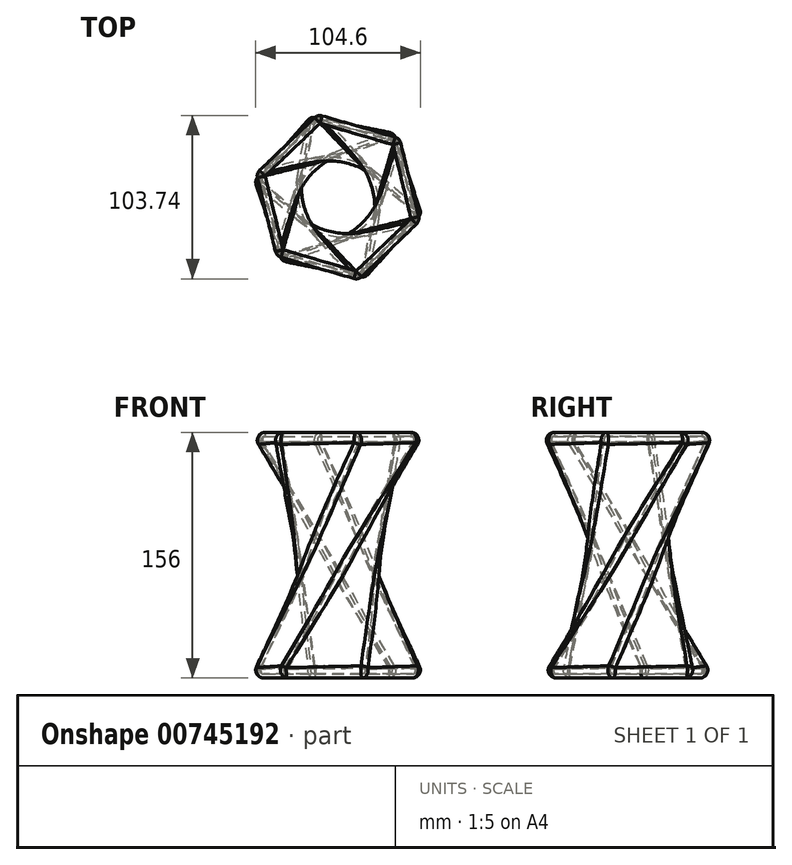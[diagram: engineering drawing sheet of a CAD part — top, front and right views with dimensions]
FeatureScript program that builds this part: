
annotation { "Feature Type Name" : "Feature", "Feature Type Description" : "" }
export const myFeature = defineFeature(function(context is Context, id is Id, definition is map)
    precondition{}
    {
        {
            var Q0;
            Q0=qCreatedBy(makeId("Top.planeOp"),FACE);
            var sketch = newSketch(context, id + "F0", { "sketchPlane" : qUnion([Q0])});
            skCircle(sketch, "E0.cCircle", {"center": v(0, 0) * mm, "radius": 49.72 * mm, "construction": true});
            skLineSegment(sketch, "E0.0", {"start": v(55.75, -13.73) * mm, "end": v(15.99, -55.14) * mm});
            skLineSegment(sketch, "E0.1", {"start": v(15.99, -55.14) * mm, "end": v(-39.76, -41.42) * mm});
            skLineSegment(sketch, "E0.2", {"start": v(-39.76, -41.42) * mm, "end": v(-55.75, 13.73) * mm});
            skLineSegment(sketch, "E0.3", {"start": v(-55.75, 13.73) * mm, "end": v(-15.99, 55.14) * mm});
            skLineSegment(sketch, "E0.4", {"start": v(-15.99, 55.14) * mm, "end": v(39.76, 41.42) * mm});
            skLineSegment(sketch, "E0.5", {"start": v(39.76, 41.42) * mm, "end": v(55.75, -13.73) * mm});
            skPoint(sketch, "E0.0.midPoint", {"position": v(35.87, -34.44) * mm});
            skSolve(sketch);
        }
        {
            var Q0;
            Q0=qCreatedBy(makeId("Top.planeOp"),FACE);
            cPlane(context, id + "F1", {"entities" : qUnion([Q0]), "cplaneType" : CPlaneType.OFFSET, "offset" : 156 * mm, "width" : 150 * mm, "height" : 150 * mm});
        }
        {
            var Q0;
            Q0=qCreatedBy(id+"F1.planeOp",FACE);
            var sketch = newSketch(context, id + "F2", { "sketchPlane" : qUnion([Q0])});
            skLineSegment(sketch, "E1.0.0", {"start": v(55.75, -13.73) * mm, "end": v(39.76, 41.42) * mm});
            skLineSegment(sketch, "E1.0.1", {"start": v(39.76, 41.42) * mm, "end": v(-15.99, 55.14) * mm});
            skLineSegment(sketch, "E1.0.2", {"start": v(-15.99, 55.14) * mm, "end": v(-55.75, 13.73) * mm});
            skLineSegment(sketch, "E1.0.3", {"start": v(-55.75, 13.73) * mm, "end": v(-39.76, -41.42) * mm});
            skLineSegment(sketch, "E1.0.4", {"start": v(-39.76, -41.42) * mm, "end": v(15.99, -55.14) * mm});
            skLineSegment(sketch, "E1.0.5", {"start": v(15.99, -55.14) * mm, "end": v(55.75, -13.73) * mm});
            skSolve(sketch);
        }
        {
            var Q0;
            Q0=makeQuery(id+"F2.imprint","IMPRINT",FACE,{"disambiguationData":[TD([[makeQuery(id+"F2.imprint","IMPRINT",EDGE,{"derivedFrom":sQuery(id+"F2.wireOp",EDGE,"E1.0.0")}),1.0]])]});
            var Q1;
            Q1=makeQuery(id+"F0.imprint","IMPRINT",FACE,{"disambiguationData":[TD([[makeQuery(id+"F0.imprint","IMPRINT",EDGE,{"derivedFrom":sQuery(id+"F0.wireOp",EDGE,"E0.0")}),-1.0]])]});
            var Q2;
            Q2=sQuery(id+"F2.wireOp",VERTEX,"E1.0.0.start");
            var Q3;
            Q3=sQuery(id+"F0.wireOp",VERTEX,"E0.2.start");
            loft(context, id + "F3", {"sheetProfilesArray" : [{ "sheetProfileEntities" : qUnion([Q0]) }, { "sheetProfileEntities" : qUnion([Q1]) }], "matchConnections" : true, "connections" : [{ "connectionEntities" : qUnion([Q2, Q3]), "connectionEdgeQueries" : qUnion([]), "connectionEdgeParameters" : [] }]});
        }
        {
            var Q0;
            Q0=makeQuery(id+"F3.opLoft","MID_CAP_EDGE",EDGE,{"disambiguationData":[OSD([sQuery(id+"F2.wireOp",EDGE,"E1.0.2"),sQuery(id+"F2.wireOp",EDGE,"E1.0.3"),sQuery(id+"F2.wireOp",EDGE,"E1.0.4")])],"capPos":0.0});
            var Q1;
            Q1=makeQuery(id+"F3.opLoft","MID_CAP_EDGE",EDGE,{"disambiguationData":[OSD([sQuery(id+"F2.wireOp",EDGE,"E1.0.3"),sQuery(id+"F2.wireOp",EDGE,"E1.0.4"),sQuery(id+"F2.wireOp",EDGE,"E1.0.5")])],"capPos":0.0});
            var Q2;
            Q2=makeQuery(id+"F3.opLoft","MID_CAP_EDGE",EDGE,{"disambiguationData":[OSD([sQuery(id+"F2.wireOp",EDGE,"E1.0.0"),sQuery(id+"F2.wireOp",EDGE,"E1.0.4"),sQuery(id+"F2.wireOp",EDGE,"E1.0.5")])],"capPos":0.0});
            var Q3;
            Q3=makeQuery(id+"F3.opLoft","MID_CAP_EDGE",EDGE,{"disambiguationData":[OSD([sQuery(id+"F2.wireOp",EDGE,"E1.0.0"),sQuery(id+"F2.wireOp",EDGE,"E1.0.1"),sQuery(id+"F2.wireOp",EDGE,"E1.0.5")])],"capPos":0.0});
            var Q4;
            Q4=makeQuery(id+"F3.opLoft","MID_CAP_EDGE",EDGE,{"disambiguationData":[OSD([sQuery(id+"F2.wireOp",EDGE,"E1.0.0"),sQuery(id+"F2.wireOp",EDGE,"E1.0.1"),sQuery(id+"F2.wireOp",EDGE,"E1.0.2")])],"capPos":0.0});
            var Q5;
            Q5=makeQuery(id+"F3.opLoft","MID_CAP_EDGE",EDGE,{"disambiguationData":[OSD([sQuery(id+"F2.wireOp",EDGE,"E1.0.1"),sQuery(id+"F2.wireOp",EDGE,"E1.0.2"),sQuery(id+"F2.wireOp",EDGE,"E1.0.3")])],"capPos":0.0});
            fillet(context, id + "F4", {"entities" : qUnion([Q0, Q1, Q2, Q3, Q4, Q5]), "radius" : 5 * mm, "tangentPropagation" : true, "allowEdgeOverflow" : false});
        }
        {
            var Q0;
            Q0=makeQuery(id+"F3.opLoft","MID_CAP_EDGE",EDGE,{"disambiguationData":[OSD([sQuery(id+"F0.wireOp",EDGE,"E0.0"),sQuery(id+"F0.wireOp",EDGE,"E0.1"),sQuery(id+"F0.wireOp",EDGE,"E0.5")])],"capPos":1.0});
            var Q1;
            Q1=makeQuery(id+"F3.opLoft","MID_CAP_EDGE",EDGE,{"disambiguationData":[OSD([sQuery(id+"F0.wireOp",EDGE,"E0.0"),sQuery(id+"F0.wireOp",EDGE,"E0.1"),sQuery(id+"F0.wireOp",EDGE,"E0.2")])],"capPos":1.0});
            var Q2;
            Q2=makeQuery(id+"F3.opLoft","MID_CAP_EDGE",EDGE,{"disambiguationData":[OSD([sQuery(id+"F0.wireOp",EDGE,"E0.1"),sQuery(id+"F0.wireOp",EDGE,"E0.2"),sQuery(id+"F0.wireOp",EDGE,"E0.3")])],"capPos":1.0});
            var Q3;
            Q3=makeQuery(id+"F3.opLoft","MID_CAP_EDGE",EDGE,{"disambiguationData":[OSD([sQuery(id+"F0.wireOp",EDGE,"E0.2"),sQuery(id+"F0.wireOp",EDGE,"E0.3"),sQuery(id+"F0.wireOp",EDGE,"E0.4")])],"capPos":1.0});
            var Q4;
            Q4=makeQuery(id+"F3.opLoft","MID_CAP_EDGE",EDGE,{"disambiguationData":[OSD([sQuery(id+"F0.wireOp",EDGE,"E0.3"),sQuery(id+"F0.wireOp",EDGE,"E0.4"),sQuery(id+"F0.wireOp",EDGE,"E0.5")])],"capPos":1.0});
            var Q5;
            Q5=makeQuery(id+"F3.opLoft","MID_CAP_EDGE",EDGE,{"disambiguationData":[OSD([sQuery(id+"F0.wireOp",EDGE,"E0.0"),sQuery(id+"F0.wireOp",EDGE,"E0.4"),sQuery(id+"F0.wireOp",EDGE,"E0.5")])],"capPos":1.0});
            var Q6;
            Q6=makeQuery(id+"F3.opLoft","SWEPT_EDGE",EDGE,{"disambiguationData":[OSD([sQuery(id+"F0.wireOp",EDGE,"E0.1"),sQuery(id+"F0.wireOp",EDGE,"E0.2"),sQuery(id+"F2.wireOp",EDGE,"E1.0.0"),sQuery(id+"F2.wireOp",EDGE,"E1.0.5")])]});
            var Q7;
            Q7=makeQuery(id+"F3.opLoft","SWEPT_EDGE",EDGE,{"disambiguationData":[OSD([sQuery(id+"F0.wireOp",EDGE,"E0.0"),sQuery(id+"F0.wireOp",EDGE,"E0.1"),sQuery(id+"F2.wireOp",EDGE,"E1.0.0"),sQuery(id+"F2.wireOp",EDGE,"E1.0.1")])]});
            var Q8;
            Q8=makeQuery(id+"F3.opLoft","SWEPT_EDGE",EDGE,{"disambiguationData":[OSD([sQuery(id+"F0.wireOp",EDGE,"E0.0"),sQuery(id+"F0.wireOp",EDGE,"E0.5"),sQuery(id+"F2.wireOp",EDGE,"E1.0.1"),sQuery(id+"F2.wireOp",EDGE,"E1.0.2")])]});
            var Q9;
            Q9=makeQuery(id+"F3.opLoft","SWEPT_EDGE",EDGE,{"disambiguationData":[OSD([sQuery(id+"F0.wireOp",EDGE,"E0.4"),sQuery(id+"F0.wireOp",EDGE,"E0.5"),sQuery(id+"F2.wireOp",EDGE,"E1.0.2"),sQuery(id+"F2.wireOp",EDGE,"E1.0.3")])]});
            var Q10;
            Q10=makeQuery(id+"F3.opLoft","SWEPT_EDGE",EDGE,{"disambiguationData":[OSD([sQuery(id+"F0.wireOp",EDGE,"E0.3"),sQuery(id+"F0.wireOp",EDGE,"E0.4"),sQuery(id+"F2.wireOp",EDGE,"E1.0.3"),sQuery(id+"F2.wireOp",EDGE,"E1.0.4")])]});
            var Q11;
            Q11=makeQuery(id+"F3.opLoft","SWEPT_EDGE",EDGE,{"disambiguationData":[OSD([sQuery(id+"F0.wireOp",EDGE,"E0.2"),sQuery(id+"F0.wireOp",EDGE,"E0.3"),sQuery(id+"F2.wireOp",EDGE,"E1.0.4"),sQuery(id+"F2.wireOp",EDGE,"E1.0.5")])]});
            fillet(context, id + "F5", {"entities" : qUnion([Q0, Q1, Q2, Q3, Q4, Q5, Q6, Q7, Q8, Q9, Q10, Q11]), "radius" : 5 * mm, "tangentPropagation" : true, "allowEdgeOverflow" : false});
        }
        {
            var Q0;
            Q0=makeQuery(id+"F3.opLoft","CAP_FACE",FACE,{"disambiguationData":[OSD([makeQuery(id+"F2.imprint","IMPRINT",FACE,{"disambiguationData":[TD([[makeQuery(id+"F2.imprint","IMPRINT",EDGE,{"derivedFrom":sQuery(id+"F2.wireOp",EDGE,"E1.0.0")}),1.0]])]})])],"isStart":true});
            shell(context, id + "F6", {"entities" : qUnion([Q0]), "thickness" : 2.5 * mm});
        }
    });
